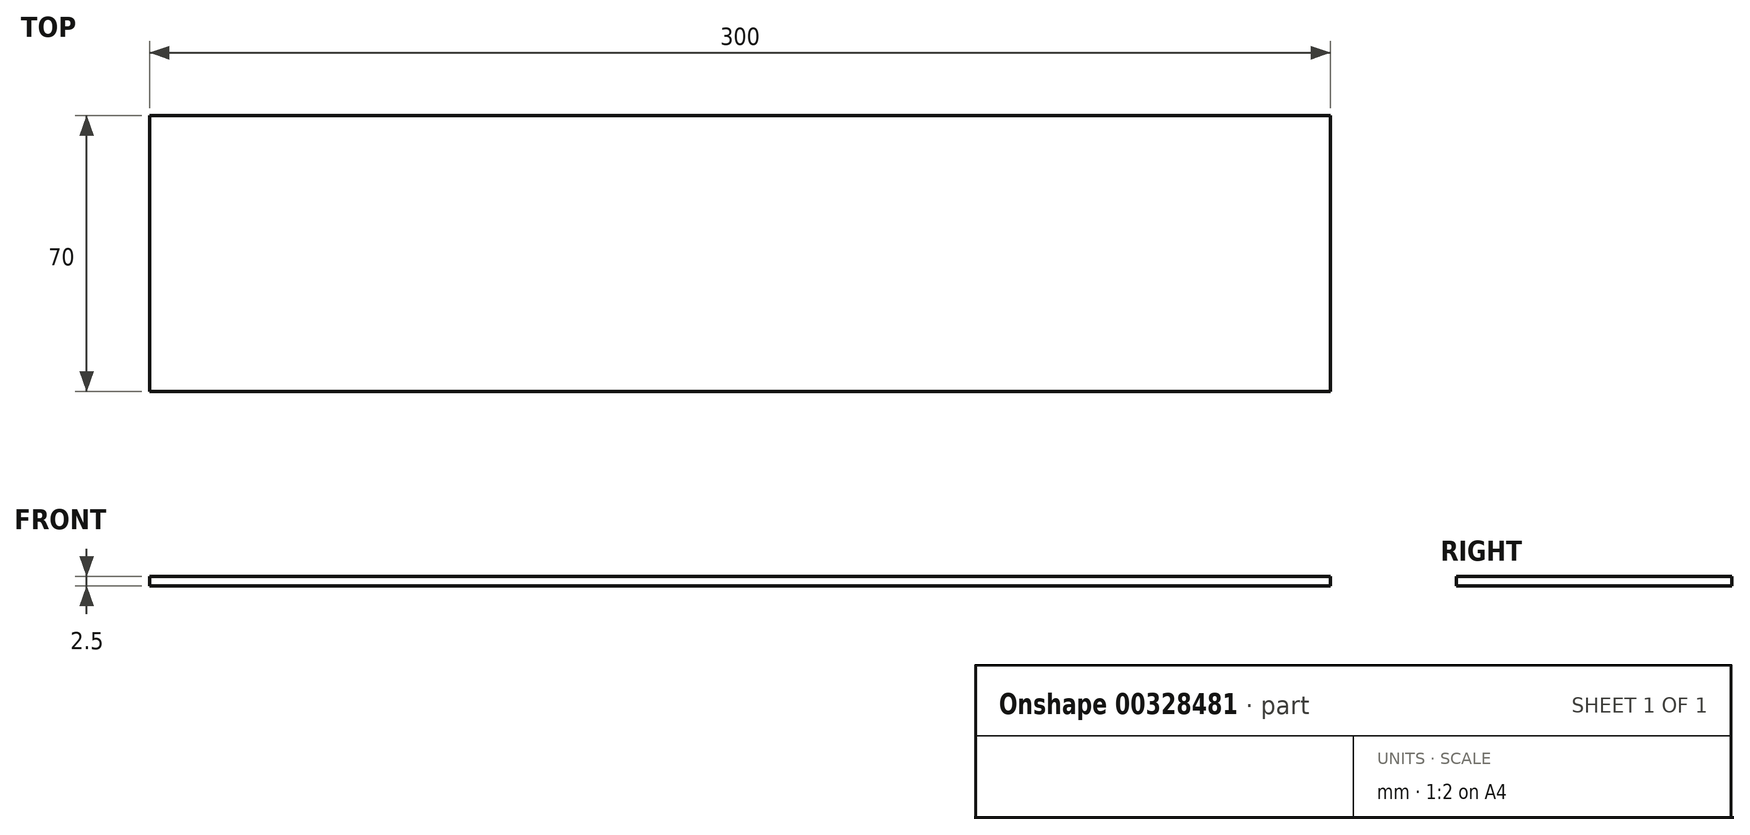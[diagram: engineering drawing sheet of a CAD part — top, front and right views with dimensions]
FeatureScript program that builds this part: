
annotation { "Feature Type Name" : "Feature", "Feature Type Description" : "" }
export const myFeature = defineFeature(function(context is Context, id is Id, definition is map)
    precondition{}
    {
        {
            var Q0;
            Q0=qCreatedBy(makeId("Top.planeOp"),FACE);
            var sketch = newSketch(context, id + "F0", { "sketchPlane" : qUnion([Q0])});
            skLineSegment(sketch, "E0.bottom", {"start": v(150, -35) * mm, "end": v(-150, -35) * mm});
            skLineSegment(sketch, "E0.top", {"start": v(150, 35) * mm, "end": v(-150, 35) * mm});
            skLineSegment(sketch, "E0.left", {"start": v(150, -35) * mm, "end": v(150, 35) * mm});
            skLineSegment(sketch, "E0.right", {"start": v(-150, -35) * mm, "end": v(-150, 35) * mm});
            skPoint(sketch, "E0.middle", {"position": v(0, 0) * mm});
            skSolve(sketch);
        }
        {
            var Q0;
            Q0=makeQuery(id+"F0.imprint","IMPRINT",FACE,{"disambiguationData":[TD([[makeQuery(id+"F0.imprint","IMPRINT",EDGE,{"derivedFrom":sQuery(id+"F0.wireOp",EDGE,"E0.bottom")}),-1.0]])]});
            extrude(context, id + "F1", {"entities" : qUnion([Q0]), "depth" : 2.5 * mm});
        }
    });
